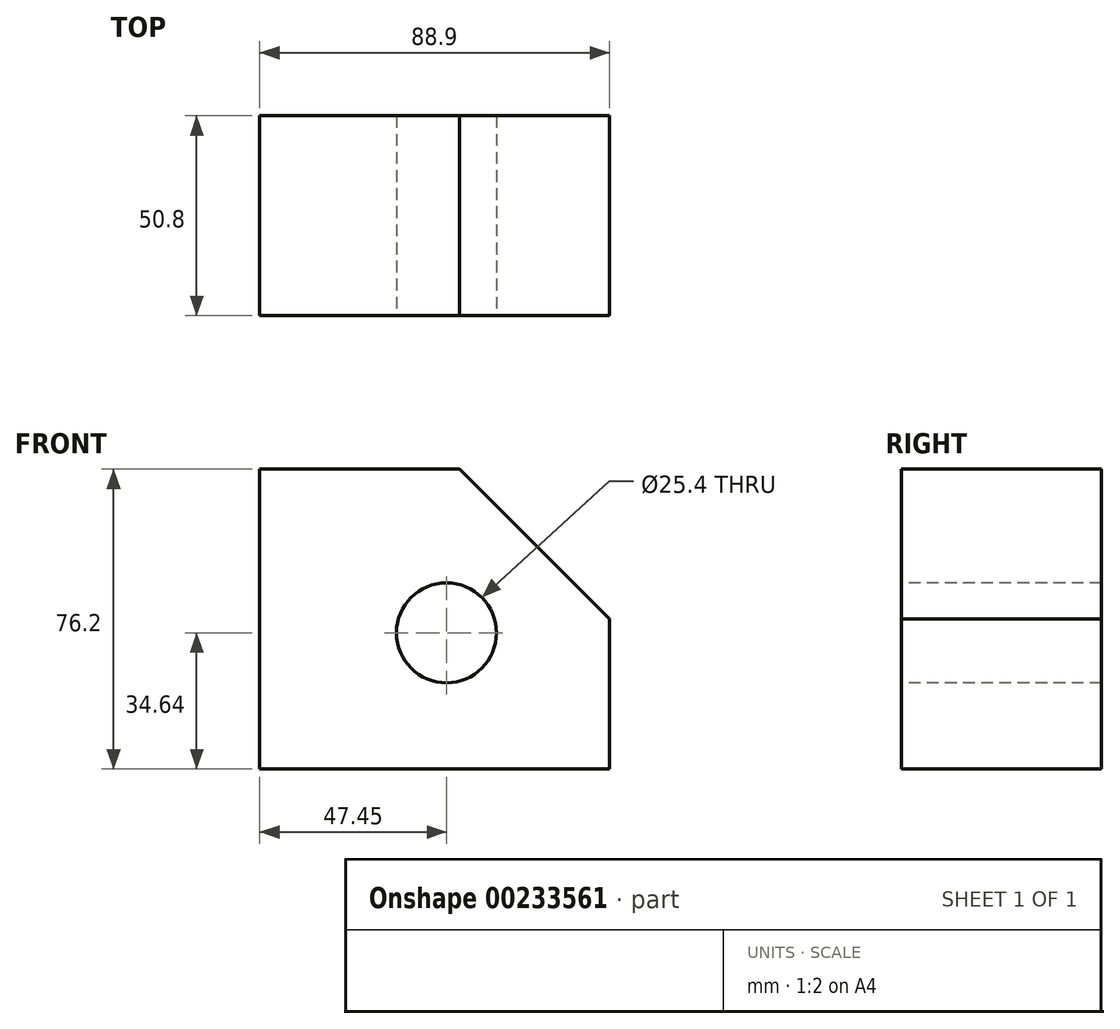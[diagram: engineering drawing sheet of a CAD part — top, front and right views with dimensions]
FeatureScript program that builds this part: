
annotation { "Feature Type Name" : "Feature", "Feature Type Description" : "" }
export const myFeature = defineFeature(function(context is Context, id is Id, definition is map)
    precondition{}
    {
        {
            var Q0;
            Q0=qCreatedBy(makeId("Front.planeOp"),FACE);
            var sketch = newSketch(context, id + "F0", { "sketchPlane" : qUnion([Q0])});
            skLineSegment(sketch, "E0.bottom", {"start": v(-47.45, 41.56) * mm, "end": v(41.45, 41.56) * mm});
            skLineSegment(sketch, "E0.top", {"start": v(-47.45, -34.64) * mm, "end": v(41.45, -34.64) * mm});
            skLineSegment(sketch, "E0.left", {"start": v(-47.45, 41.56) * mm, "end": v(-47.45, -34.64) * mm});
            skLineSegment(sketch, "E0.right", {"start": v(41.45, 41.56) * mm, "end": v(41.45, -34.64) * mm});
            skSolve(sketch);
        }
        {
            var Q0;
            Q0 = qSketchRegion(id + "F0", true);
            extrude(context, id + "F1", {"entities" : qUnion([Q0]), "depth" : 50.8 * mm});
        }
        {
            var Q0;
            Q0=makeQuery(id+"F1.opExtrude","SWEPT_EDGE",EDGE,{"disambiguationData":[OSD([sQuery(id+"F0.wireOp",EDGE,"E0.bottom"),sQuery(id+"F0.wireOp",EDGE,"E0.right")])]});
            chamfer(context, id + "F2", {"entities" : qUnion([Q0]), "width" : 38.1 * mm, "tangentPropagation" : true});
        }
        {
            var Q0;
            Q0=makeQuery(id+"F1.opExtrude","CAP_FACE",FACE,{"disambiguationData":[OSD([sQuery(id+"F0.wireOp",EDGE,"E0.bottom"),sQuery(id+"F0.wireOp",EDGE,"E0.top"),sQuery(id+"F0.wireOp",EDGE,"E0.left"),sQuery(id+"F0.wireOp",EDGE,"E0.right")])],"isStart":false});
            var sketch = newSketch(context, id + "F3", { "sketchPlane" : qUnion([Q0])});
            skCircle(sketch, "E1", {"center": v(0, 0) * mm, "radius": 12.7 * mm});
            skSolve(sketch);
        }
        {
            var Q0;
            Q0=makeQuery(id+"F3.imprint","IMPRINT",FACE,{"disambiguationData":[TD([[makeQuery(id+"F3.imprint","IMPRINT",EDGE,{"derivedFrom":sQuery(id+"F3.wireOp",EDGE,"E1")}),1.0]])]});
            extrude(context, id + "F4", {"entities" : qUnion([Q0]), "operationType" : NewBodyOperationType.REMOVE, "oppositeDirection" : true, "depth" : 50.8 * mm});
        }
    });
